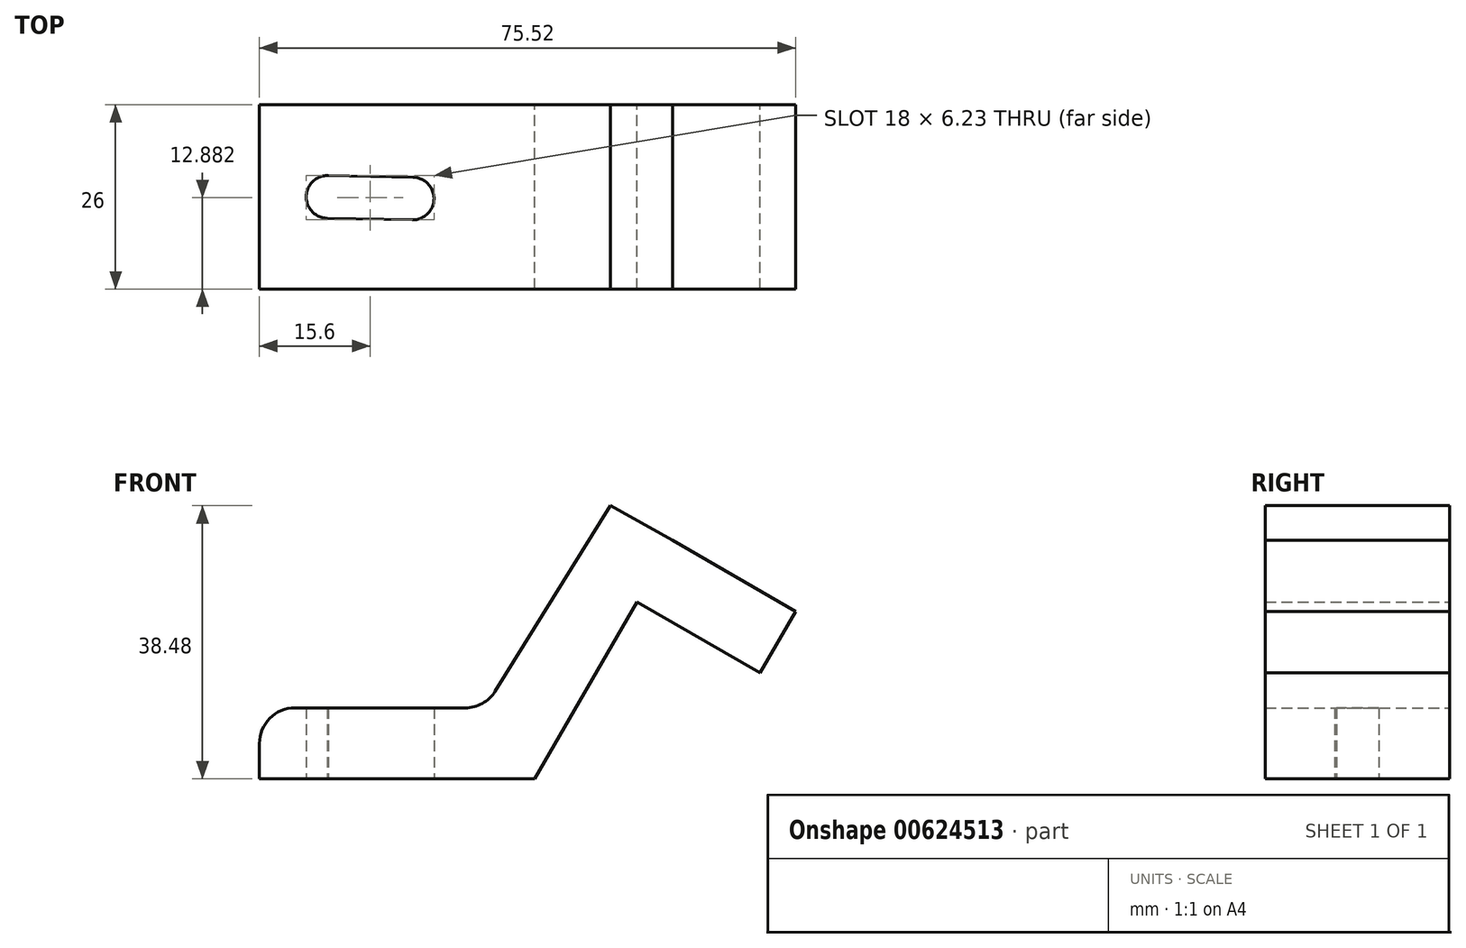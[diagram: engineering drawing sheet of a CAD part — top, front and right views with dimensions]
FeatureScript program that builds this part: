
annotation { "Feature Type Name" : "Feature", "Feature Type Description" : "" }
export const myFeature = defineFeature(function(context is Context, id is Id, definition is map)
    precondition{}
    {
        {
            var Q0;
            Q0=qCreatedBy(makeId("Front.planeOp"),FACE);
            var sketch = newSketch(context, id + "F0", { "sketchPlane" : qUnion([Q0])});
            skLineSegment(sketch, "E0", {"start": v(-9.6, 4.21) * mm, "end": v(29.2, 4.21) * mm});
            skLineSegment(sketch, "E1", {"start": v(23.63, 16.57) * mm, "end": v(39.87, 42.7) * mm});
            skPoint(sketch, "E2.end.orphan", {"position": v(50.6, 44.78) * mm});
            skLineSegment(sketch, "E3", {"start": v(29.2, 4.21) * mm, "end": v(48.6, 37.81) * mm});
            skLineSegment(sketch, "E4", {"start": v(48.6, 37.81) * mm, "end": v(39.87, 42.7) * mm});
            skLineSegment(sketch, "E5", {"start": v(48.6, 37.81) * mm, "end": v(65.92, 27.81) * mm});
            skLineSegment(sketch, "E6", {"start": v(65.92, 27.81) * mm, "end": v(60.92, 19.15) * mm});
            skLineSegment(sketch, "E7", {"start": v(60.92, 19.15) * mm, "end": v(43.6, 29.15) * mm});
            skLineSegment(sketch, "E8", {"start": v(-9.6, 9.21) * mm, "end": v(-9.6, 4.21) * mm});
            skLineSegment(sketch, "E9", {"start": v(-4.6, 14.21) * mm, "end": v(19.38, 14.21) * mm});
            skArc(sketch, "E10.filletArc", {"start": v(-4.6, 14.21) * mm, "mid": v(-8.14, 12.75) * mm, "end": v(-9.6, 9.21) * mm});
            skArc(sketch, "E11.filletArc", {"start": v(19.38, 14.21) * mm, "mid": v(21.81, 14.84) * mm, "end": v(23.63, 16.57) * mm});
            skSolve(sketch);
        }
        {
            var Q0;
            Q0 = qSketchRegion(id + "F0", true);
            var Q1;
            {var subQ3=sQuery(id+"F0.wireOp",EDGE,"E0");Q1=makeQuery(id+"F0.imprint","IMPRINT",FACE,{"disambiguationData":[TD([[makeQuery(id+"F0.imprint","IMPRINT",EDGE,{"derivedFrom":subQ3}),1.0]])]});}
            extrude(context, id + "F1", {"entities" : qUnion([Q0, Q1]), "depth" : 26 * mm, "offsetDistance" : 25 * mm});
        }
        {
            var Q0;
            Q0=qCreatedBy(makeId("Top.planeOp"),FACE);
            var sketch = newSketch(context, id + "F2", { "sketchPlane" : qUnion([Q0])});
            skCircle(sketch, "E12", {"center": v(0, -13) * mm, "radius": 3 * mm});
            skCircle(sketch, "E13", {"center": v(12, -13.23) * mm, "radius": 3 * mm});
            skLineSegment(sketch, "E14", {"start": v(0, -16) * mm, "end": v(11.94, -16.23) * mm});
            skLineSegment(sketch, "E15", {"start": v(0, -10) * mm, "end": v(12.06, -10.23) * mm});
            skSolve(sketch);
        }
        {
            var Q0;
            Q0 = qSketchRegion(id + "F2", true);
            extrude(context, id + "F3", {"entities" : qUnion([Q0]), "operationType" : NewBodyOperationType.REMOVE, "endBound" : BoundingType.THROUGH_ALL, "depth" : 25 * mm, "offsetDistance" : 25 * mm});
        }
    });
